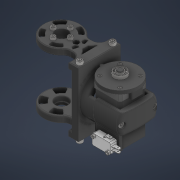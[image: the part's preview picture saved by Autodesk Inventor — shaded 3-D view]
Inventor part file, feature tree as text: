
AUTODESK INVENTOR PART (.ipt)
format: ipt  version: 2022 (Build 260153070, 153G)  size: 4,098,560 bytes
history: native  units: mm
features: other x41, projected_geometry x4, extrude x1, sketch x1
ambient origin geometry x8: Origin, YZ Plane, XZ Plane, XY Plane, X Axis, Y Axis, Z Axis, Center Point
bodies: Solid1 (feature_tree)
feature tree (47):
  other  "short_link.iam"
  other  "Stepper_nema17.ipt:1"
  other  "reductor.iam:1::Stator_encoder_lite.ipt:1"
  other  "reductor.iam:1::Center_encoder_lite.ipt:1"
  other  "reductor.iam:1::Excenter_lite.ipt:1"
  other  "reductor.iam:1::Stator_lite.ipt:1"
  other  "reductor.iam:1::Disk_lite.ipt:1"
  other  "reductor.iam:1::DIN 625 - T1 619/8 - 8 x 19 x 6:1"
  other  "reductor.iam:1::Center_lite.ipt:1"
  other  "reductor.iam:1::DIN 625 - T1 619/8 - 8 x 19 x 6:2"
  other  "reductor.iam:1::Rotor_lite.ipt:1"
  other  "reductor.iam:1::Housing_lite.ipt:1"
  other  "reductor.iam:1::Board.ipt:1"
  other  "reductor.iam:1::Magnet.ipt:1"
  other  "Stepper_holder_1_lite.ipt:1"
  other  "Bearing_back_lite.ipt:1"
  other  "Forearm_short_2.ipt:1"
  other  "Forearm_short_1.ipt:1"
  other  "DIN 625 - T1 619/8 - 8 x 19 x 6:1"
  other  "Stepper_bracket_1_lite.ipt:1"
  other  "DIN 912 - replaced by DIN EN ISO 4762 M3 x 25:1"
  other  "DIN 912 - replaced by DIN EN ISO 4762 M3 x 25:2"
  other  "DIN 912 - replaced by DIN EN ISO 4762 M3 x 25:3"
  other  "DIN 912 - replaced by DIN EN ISO 4762 M3 x 25:4"
  other  "DIN 912 - replaced by DIN EN ISO 4762 M3 x 30:1"
  other  "DIN 912 - replaced by DIN EN ISO 4762 M3 x 30:4"
  other  "DIN 912 - replaced by DIN EN ISO 4762 M3 x 30:2"
  other  "DIN 912 - replaced by DIN EN ISO 4762 M3 x 30:3"
  other  "DIN 912 - replaced by DIN EN ISO 4762 M4 x 16:1"
  other  "DIN 912 - replaced by DIN EN ISO 4762 M4 x 16:2"
  other  "DIN 912 - replaced by DIN EN ISO 4762 M4 x 16:3"
  other  "DIN 912 - replaced by DIN EN ISO 4762 M4 x 16:4"
  other  "DIN 912 - replaced by DIN EN ISO 4762 M5 x 16:1"
  other  "DIN 912 - replaced by DIN EN ISO 4762 M5 x 16:2"
  other  "DIN 912 - replaced by DIN EN ISO 4762 M5 x 16:4"
  other  "DIN 912 - replaced by DIN EN ISO 4762 M5 x 16:3"
  other  "DIN 912 - replaced by DIN EN ISO 4762 M5 x 40:2"
  other  "DIN 912 - replaced by DIN EN ISO 4762 M5 x 40:1"
  other  "Limit_switch.ipt:1"
  other  "DIN 912 - replaced by DIN EN ISO 4762 M3 x 12:1"
  other  "DIN 912 - replaced by DIN EN ISO 4762 M3 x 12:2"
  extrude  "Extrusion1"  Depth=10.0mm TaperAngle=0.0deg
  sketch  "Sketch1"  dims[d0=10.0mm d1=10.0mm d2=0.0mm]
  projected_geometry  "Projected Loop1"
  projected_geometry  "Projected Loop2"
  projected_geometry  "Projected Loop3"
  projected_geometry  "Projected Loop4"
